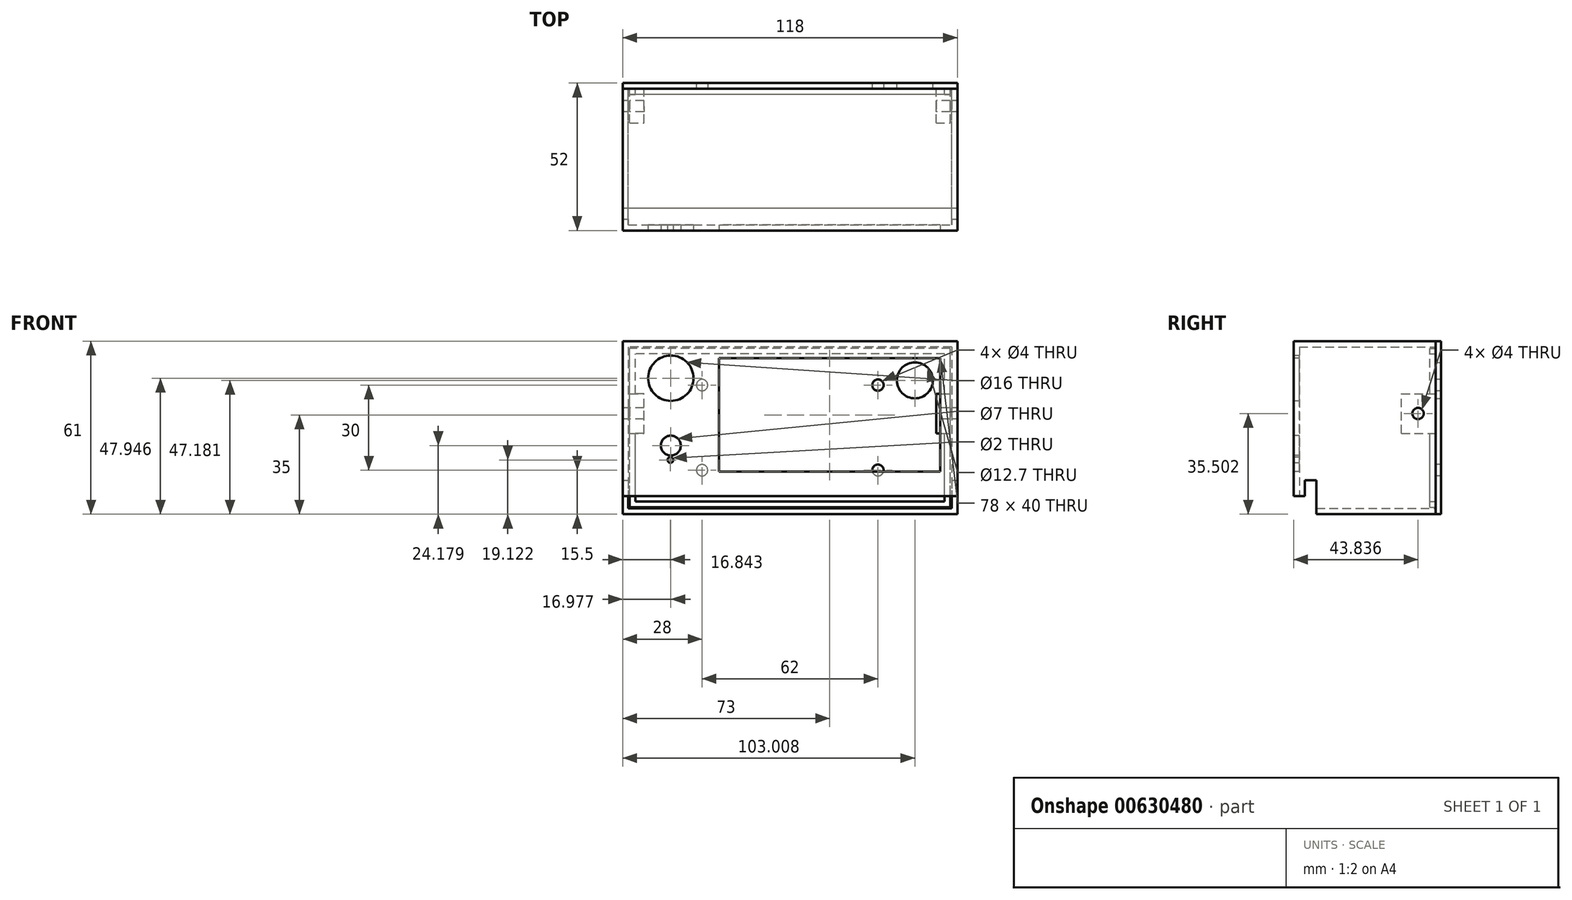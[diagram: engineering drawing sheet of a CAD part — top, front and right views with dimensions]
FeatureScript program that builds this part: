
annotation { "Feature Type Name" : "Feature", "Feature Type Description" : "" }
export const myFeature = defineFeature(function(context is Context, id is Id, definition is map)
    precondition{}
    {
        {
            var Q0;
            Q0=qCreatedBy(makeId("Top.planeOp"),FACE);
            var sketch = newSketch(context, id + "F0", { "sketchPlane" : qUnion([Q0])});
            skLineSegment(sketch, "E0.bottom", {"start": v(59, -25) * mm, "end": v(-59, -25) * mm});
            skLineSegment(sketch, "E0.top", {"start": v(59, 25) * mm, "end": v(-59, 25) * mm});
            skLineSegment(sketch, "E0.left", {"start": v(59, -25) * mm, "end": v(59, 25) * mm});
            skLineSegment(sketch, "E0.right", {"start": v(-59, -25) * mm, "end": v(-59, 25) * mm});
            skPoint(sketch, "E0.middle", {"position": v(0, 0) * mm});
            skSolve(sketch);
        }
        {
            var Q0;
            Q0 = qSketchRegion(id + "F0", true);
            extrude(context, id + "F1", {"entities" : qUnion([Q0]), "depth" : 61 * mm, "offsetDistance" : 25 * mm});
        }
        {
            var Q0;
            Q0=makeQuery(id+"F1.opExtrude","SWEPT_FACE",FACE,{"disambiguationData":[OSD([sQuery(id+"F0.wireOp",EDGE,"E0.bottom")])]});
            var sketch = newSketch(context, id + "F2", { "sketchPlane" : qUnion([Q0])});
            skLineSegment(sketch, "E1", {"start": v(59, 0) * mm, "end": v(53, 0) * mm});
            skLineSegment(sketch, "E2.bottom", {"start": v(53, 15) * mm, "end": v(-25, 15) * mm});
            skLineSegment(sketch, "E2.top", {"start": v(53, 55) * mm, "end": v(-25, 55) * mm});
            skLineSegment(sketch, "E2.left", {"start": v(53, 15) * mm, "end": v(53, 55) * mm});
            skLineSegment(sketch, "E2.right", {"start": v(-25, 15) * mm, "end": v(-25, 55) * mm});
            skCircle(sketch, "E3", {"center": v(-42.02, 24.18) * mm, "radius": 12.03 * mm});
            skCircle(sketch, "E4", {"center": v(-42.02, 24.18) * mm, "radius": 3.5 * mm});
            skCircle(sketch, "E5", {"center": v(-42.02, 47.95) * mm, "radius": 8 * mm});
            skCircle(sketch, "E6", {"center": v(-42.02, 24.18) * mm, "radius": 9.14 * mm});
            skSolve(sketch);
        }
        {
            var Q0;
            Q0=makeQuery(id+"F4.boolean.opBoolean","COPY",FACE,{"derivedFrom":makeQuery(id+"F4.opExtrude","SWEPT_FACE",FACE,{"disambiguationData":[OSD([sQuery(id+"F2.wireOp",EDGE,"E2.right")])]})});
            var Q1;
            Q1=makeQuery(id+"F1.opExtrude","SWEPT_FACE",FACE,{"disambiguationData":[OSD([sQuery(id+"F0.wireOp",EDGE,"E0.top")])]});
            shell(context, id + "F3", {"entities" : qUnion([Q0, Q1]), "thickness" : 2 * mm});
        }
        {
            var Q0;
            Q0=makeQuery(id+"F2.imprint","IMPRINT",FACE,{"disambiguationData":[TD([[makeQuery(id+"F2.imprint","IMPRINT",EDGE,{"derivedFrom":sQuery(id+"F2.wireOp",EDGE,"E5")}),1.0]])]});
            var Q1;
            Q1=makeQuery(id+"F2.imprint","IMPRINT",FACE,{"disambiguationData":[TD([[makeQuery(id+"F2.imprint","IMPRINT",EDGE,{"derivedFrom":sQuery(id+"F2.wireOp",EDGE,"E4")}),1.0]])]});
            var Q2;
            Q2=makeQuery(id+"F2.imprint","IMPRINT",FACE,{"disambiguationData":[TD([[makeQuery(id+"F2.imprint","IMPRINT",EDGE,{"derivedFrom":sQuery(id+"F2.wireOp",EDGE,"E2.bottom")}),-1.0]])]});
            extrude(context, id + "F4", {"entities" : qUnion([Q0, Q1, Q2]), "operationType" : NewBodyOperationType.REMOVE, "oppositeDirection" : true, "depth" : 48 * mm, "offsetDistance" : 25 * mm});
        }
        {
            var Q0;
            Q0=makeQuery(id+"F1.opExtrude","SWEPT_FACE",FACE,{"disambiguationData":[OSD([sQuery(id+"F0.wireOp",EDGE,"E0.left")])]});
            var sketch = newSketch(context, id + "F5", { "sketchPlane" : qUnion([Q0])});
            skLineSegment(sketch, "E7", {"start": v(-25, 0) * mm, "end": v(-21, 0) * mm});
            skLineSegment(sketch, "E8", {"start": v(-21, 0) * mm, "end": v(-21, 5) * mm});
            skLineSegment(sketch, "E9.top", {"start": v(-21, 0) * mm, "end": v(-17, 0) * mm});
            skLineSegment(sketch, "E9.left", {"start": v(-21, 5) * mm, "end": v(-21, 0) * mm});
            skLineSegment(sketch, "E9.right", {"start": v(-17, 5) * mm, "end": v(-17, 0) * mm});
            skLineSegment(sketch, "E10", {"start": v(-21, 5) * mm, "end": v(-21, 12) * mm});
            skLineSegment(sketch, "E11", {"start": v(-17, 5) * mm, "end": v(-17, 12) * mm});
            skLineSegment(sketch, "E12", {"start": v(-17, 12) * mm, "end": v(-21, 12) * mm});
            skSolve(sketch);
        }
        {
            var Q0;
            Q0=makeQuery(id+"F5.imprint","IMPRINT",FACE,{"disambiguationData":[TD([[makeQuery(id+"F5.imprint","IMPRINT",EDGE,{"derivedFrom":sQuery(id+"F5.wireOp",EDGE,"E9.bottom")}),-1.0]])]});
            var Q1;
            Q1=makeQuery(id+"F5.imprint","IMPRINT",FACE,{"disambiguationData":[TD([[makeQuery(id+"F5.imprint","IMPRINT",EDGE,{"derivedFrom":sQuery(id+"F5.wireOp",EDGE,"E9.top")}),1.0]])]});
            extrude(context, id + "F6", {"entities" : qUnion([Q0, Q1]), "operationType" : NewBodyOperationType.REMOVE, "oppositeDirection" : true, "depth" : 193.9 * mm, "offsetDistance" : 25 * mm});
        }
        {
            var Q0;
            {var subQ0=sQuery(id+"F0.wireOp",EDGE,"E0.bottom");var subQ1=sQuery(id+"F0.wireOp",EDGE,"E0.right");var subQ2=sQuery(id+"F0.wireOp",EDGE,"E0.left");Q0=makeQuery(id+"F6.boolean.opBoolean","SPLIT",FACE,{"disambiguationData":[TD([makeQuery(id+"F1.opExtrude","SWEPT_FACE",FACE,{"disambiguationData":[OSD([subQ0])]})])],"derivedFrom":makeQuery(id+"F1.opExtrude","CAP_FACE",FACE,{"disambiguationData":[OSD([subQ0,sQuery(id+"F0.wireOp",EDGE,"E0.top"),subQ2,subQ1])],"isStart":true})});}
            var sketch = newSketch(context, id + "F7", { "sketchPlane" : qUnion([Q0])});
            skSolve(sketch);
        }
        {
            var Q0;
            Q0 = qSketchRegion(id + "F7", true);
            var Q1;
            {var subQ0=sQuery(id+"F0.wireOp",EDGE,"E0.bottom");Q1=makeQuery(id+"F7.imprint","IMPRINT",FACE,{"disambiguationData":[TD([[makeQuery(id+"F7.imprint","IMPRINT",EDGE,{"derivedFrom":makeQuery(id+"F1.opExtrude","CAP_EDGE",EDGE,{"disambiguationData":[OSD([subQ0])],"isStart":true})}),1.0]])]});}
            extrude(context, id + "F8", {"entities" : qUnion([Q0, Q1]), "operationType" : NewBodyOperationType.REMOVE, "oppositeDirection" : true, "depth" : 6.4 * mm, "offsetDistance" : 25 * mm});
        }
        {
            var Q0;
            Q0=makeQuery(id+"F1.opExtrude","SWEPT_FACE",FACE,{"disambiguationData":[OSD([sQuery(id+"F0.wireOp",EDGE,"E0.top")])]});
            var sketch = newSketch(context, id + "F9", { "sketchPlane" : qUnion([Q0])});
            skLineSegment(sketch, "E13.bottom", {"start": v(-59, 61) * mm, "end": v(59, 61) * mm});
            skLineSegment(sketch, "E13.top", {"start": v(-59, 0) * mm, "end": v(59, 0) * mm});
            skLineSegment(sketch, "E13.left", {"start": v(-59, 61) * mm, "end": v(-59, 0) * mm});
            skLineSegment(sketch, "E13.right", {"start": v(59, 61) * mm, "end": v(59, 0) * mm});
            skSolve(sketch);
        }
        {
            var Q0;
            Q0 = qSketchRegion(id + "F9", true);
            extrude(context, id + "F10", {"entities" : qUnion([Q0]), "depth" : 2 * mm, "offsetDistance" : 25 * mm});
        }
        {
            var Q0;
            Q0=makeQuery(id+"F10.opExtrude","CAP_FACE",FACE,{"disambiguationData":[OSD([sQuery(id+"F9.wireOp",EDGE,"E13.bottom"),sQuery(id+"F9.wireOp",EDGE,"E13.top"),sQuery(id+"F9.wireOp",EDGE,"E13.left"),sQuery(id+"F9.wireOp",EDGE,"E13.right")])],"isStart":false});
            shell(context, id + "F11", {"entities" : qUnion([Q0]), "thickness" : 2 * mm});
        }
        {
            var Q0;
            Q0=makeQuery(id+"F10.opExtrude","CAP_FACE",FACE,{"disambiguationData":[OSD([sQuery(id+"F9.wireOp",EDGE,"E13.bottom"),sQuery(id+"F9.wireOp",EDGE,"E13.top"),sQuery(id+"F9.wireOp",EDGE,"E13.left"),sQuery(id+"F9.wireOp",EDGE,"E13.right")])],"isStart":true});
            var sketch = newSketch(context, id + "F12", { "sketchPlane" : qUnion([Q0])});
            skLineSegment(sketch, "E14.bottom", {"start": v(-59, 61) * mm, "end": v(-56.5, 61) * mm});
            skLineSegment(sketch, "E14.top", {"start": v(-59, 58.5) * mm, "end": v(-56.5, 58.5) * mm});
            skLineSegment(sketch, "E14.left", {"start": v(-59, 61) * mm, "end": v(-59, 58.5) * mm});
            skLineSegment(sketch, "E14.right", {"start": v(-56.5, 61) * mm, "end": v(-56.5, 58.5) * mm});
            skLineSegment(sketch, "E15.bottom", {"start": v(59, 0) * mm, "end": v(56.5, 0) * mm});
            skLineSegment(sketch, "E15.top", {"start": v(59, 2.5) * mm, "end": v(56.5, 2.5) * mm});
            skLineSegment(sketch, "E15.left", {"start": v(59, 0) * mm, "end": v(59, 2.5) * mm});
            skLineSegment(sketch, "E15.right", {"start": v(56.5, 0) * mm, "end": v(56.5, 2.5) * mm});
            skLineSegment(sketch, "E16.bottom", {"start": v(56.5, 2.5) * mm, "end": v(-56.5, 2.5) * mm});
            skLineSegment(sketch, "E16.top", {"start": v(56.5, 58.5) * mm, "end": v(-56.5, 58.5) * mm});
            skLineSegment(sketch, "E16.left", {"start": v(56.5, 2.5) * mm, "end": v(56.5, 58.5) * mm});
            skLineSegment(sketch, "E16.right", {"start": v(-56.5, 2.5) * mm, "end": v(-56.5, 58.5) * mm});
            skSolve(sketch);
        }
        {
            var Q0;
            Q0=makeQuery(id+"F12.imprint","IMPRINT",FACE,{"disambiguationData":[TD([[makeQuery(id+"F12.imprint","IMPRINT",EDGE,{"derivedFrom":sQuery(id+"F12.wireOp",EDGE,"E16.bottom")}),-1.0]])]});
            extrude(context, id + "F13", {"entities" : qUnion([Q0]), "operationType" : NewBodyOperationType.ADD, "depth" : 2 * mm, "offsetDistance" : 25 * mm});
        }
        {
            var Q0;
            Q0=makeQuery(id+"F13.opExtrude","CAP_FACE",FACE,{"disambiguationData":[OSD([sQuery(id+"F12.wireOp",EDGE,"E16.bottom"),sQuery(id+"F12.wireOp",EDGE,"E16.top"),sQuery(id+"F12.wireOp",EDGE,"E16.left"),sQuery(id+"F12.wireOp",EDGE,"E16.right")])],"isStart":false});
            shell(context, id + "F14", {"entities" : qUnion([Q0]), "thickness" : 2 * mm});
        }
        {
            var Q0;
            Q0=makeQuery(id+"F14.opShell","OFFSET_FACE",FACE,{"disambiguationData":[OSD([sQuery(id+"F9.wireOp",EDGE,"E13.bottom"),sQuery(id+"F9.wireOp",EDGE,"E13.top"),sQuery(id+"F9.wireOp",EDGE,"E13.left"),sQuery(id+"F9.wireOp",EDGE,"E13.right")])]});
            var sketch = newSketch(context, id + "F15", { "sketchPlane" : qUnion([Q0])});
            skPoint(sketch, "E17.endSnap0", {"position": v(0, 4.5) * mm});
            skLineSegment(sketch, "E18.bottom", {"start": v(31, 15.5) * mm, "end": v(-31, 15.5) * mm});
            skLineSegment(sketch, "E18.top", {"start": v(31, 45.5) * mm, "end": v(-31, 45.5) * mm});
            skLineSegment(sketch, "E18.left", {"start": v(31, 15.5) * mm, "end": v(31, 45.5) * mm});
            skLineSegment(sketch, "E18.right", {"start": v(-31, 15.5) * mm, "end": v(-31, 45.5) * mm});
            skPoint(sketch, "E18.middle", {"position": v(0, 30.5) * mm});
            skSolve(sketch);
        }
        {
            var Q0;
            Q0=sQuery(id+"F15.wireOp",VERTEX,"E18.right.end");
            var Q1;
            Q1=sQuery(id+"F15.wireOp",VERTEX,"E18.left.end");
            var Q2;
            Q2=sQuery(id+"F15.wireOp",VERTEX,"E18.bottom.start");
            var Q3;
            Q3=sQuery(id+"F15.wireOp",VERTEX,"E18.bottom.end");
            var Q4;
            Q4=makeQuery(id+"F10.opExtrude","SWEPT_BODY",BODY,{"disambiguationData":[OSD([sQuery(id+"F9.wireOp",EDGE,"E13.bottom"),sQuery(id+"F9.wireOp",EDGE,"E13.top"),sQuery(id+"F9.wireOp",EDGE,"E13.left"),sQuery(id+"F9.wireOp",EDGE,"E13.right")])]});
            hole(context, id + "F16", {"style" : HoleStyle.SIMPLE, "endStyle" : HoleEndStyle.THROUGH, "holeDiameter" : 4 * mm, "majorDiameter" : 5 * mm, "isTappedThrough" : true, "tappedDepth" : 12 * mm, "tapClearance" : 3, "startFromSketch" : true, "locations" : qUnion([Q0, Q1, Q2, Q3]), "scope" : qUnion([Q4])});
        }
        {
            var Q0;
            Q0=makeQuery(id+"F13.opExtrude","CAP_FACE",FACE,{"disambiguationData":[OSD([sQuery(id+"F12.wireOp",EDGE,"E16.bottom"),sQuery(id+"F12.wireOp",EDGE,"E16.top"),sQuery(id+"F12.wireOp",EDGE,"E16.left"),sQuery(id+"F12.wireOp",EDGE,"E16.right")])],"isStart":false});
            var sketch = newSketch(context, id + "F17", { "sketchPlane" : qUnion([Q0])});
            skLineSegment(sketch, "E19.bottom", {"start": v(-56.5, 30.5) * mm, "end": v(56.5, 30.5) * mm});
            skLineSegment(sketch, "E19.top", {"start": v(-56.5, 40.86) * mm, "end": v(56.5, 40.86) * mm});
            skLineSegment(sketch, "E19.left", {"start": v(-56.5, 30.5) * mm, "end": v(-56.5, 40.86) * mm});
            skLineSegment(sketch, "E19.right", {"start": v(56.5, 30.5) * mm, "end": v(56.5, 40.86) * mm});
            skSolve(sketch);
        }
        {
            var Q0;
            {var subQ0=sQuery(id+"F17.wireOp",EDGE,"E19.left");Q0=makeQuery(id+"F17.imprint","IMPRINT",FACE,{"disambiguationData":[TD([[makeQuery(id+"F17.imprint","IMPRINT",EDGE,{"derivedFrom":subQ0}),-1.0]])]});}
            var Q1;
            {var subQ0=sQuery(id+"F17.wireOp",EDGE,"E19.right");Q1=makeQuery(id+"F17.imprint","IMPRINT",FACE,{"disambiguationData":[TD([[makeQuery(id+"F17.imprint","IMPRINT",EDGE,{"derivedFrom":subQ0}),1.0]])]});}
            extrude(context, id + "F18", {"entities" : qUnion([Q0, Q1]), "operationType" : NewBodyOperationType.ADD, "depth" : 10 * mm, "offsetDistance" : 25 * mm});
        }
        {
            var Q0;
            {var subQ0=sQuery(id+"F12.wireOp",EDGE,"E16.right");Q0=makeQuery(id+"F18.boolean.opBoolean","MERGE",FACE,{"derivedFrom":[makeQuery(id+"F14.opShell","OFFSET_FACE",FACE,{"disambiguationData":[OSD([subQ0])]}),makeQuery(id+"F18.opExtrude","SWEPT_FACE",FACE,{"disambiguationData":[OSD([subQ0])]})]});}
            var sketch = newSketch(context, id + "F19", { "sketchPlane" : qUnion([Q0])});
            skLineSegment(sketch, "E20.bottom", {"start": v(13, 40.86) * mm, "end": v(25, 40.86) * mm});
            skLineSegment(sketch, "E20.top", {"start": v(13, 30.5) * mm, "end": v(25, 30.5) * mm});
            skLineSegment(sketch, "E20.left", {"start": v(13, 40.86) * mm, "end": v(13, 30.5) * mm});
            skLineSegment(sketch, "E20.right", {"start": v(25, 40.86) * mm, "end": v(25, 30.5) * mm});
            skSolve(sketch);
        }
        {
            var Q0;
            {var subQ14=sQuery(id+"F19.wireOp",EDGE,"E20.left");Q0=makeQuery(id+"F19.imprint","IMPRINT",FACE,{"disambiguationData":[TD([[makeQuery(id+"F19.imprint","IMPRINT",EDGE,{"derivedFrom":subQ14}),-1.0]])]});}
            extrude(context, id + "F20", {"entities" : qUnion([Q0]), "operationType" : NewBodyOperationType.ADD, "depth" : 1 * mm, "offsetDistance" : 25 * mm});
        }
        {
            var Q0;
            {var subQ0=sQuery(id+"F12.wireOp",EDGE,"E16.left");Q0=makeQuery(id+"F18.boolean.opBoolean","MERGE",FACE,{"derivedFrom":[makeQuery(id+"F14.opShell","OFFSET_FACE",FACE,{"disambiguationData":[OSD([subQ0])]}),makeQuery(id+"F18.opExtrude","SWEPT_FACE",FACE,{"disambiguationData":[OSD([subQ0])]})]});}
            var sketch = newSketch(context, id + "F21", { "sketchPlane" : qUnion([Q0])});
            skLineSegment(sketch, "E21.bottom", {"start": v(-13, 40.86) * mm, "end": v(-25, 40.86) * mm});
            skLineSegment(sketch, "E21.top", {"start": v(-13, 30.5) * mm, "end": v(-25, 30.5) * mm});
            skLineSegment(sketch, "E21.left", {"start": v(-13, 40.86) * mm, "end": v(-13, 30.5) * mm});
            skLineSegment(sketch, "E21.right", {"start": v(-25, 40.86) * mm, "end": v(-25, 30.5) * mm});
            skSolve(sketch);
        }
        {
            var Q0;
            Q0 = qSketchRegion(id + "F21", true);
            extrude(context, id + "F22", {"entities" : qUnion([Q0]), "operationType" : NewBodyOperationType.ADD, "depth" : 1 * mm, "offsetDistance" : 25 * mm});
        }
        {
            var Q0;
            Q0=makeQuery(id+"F20.opExtrude","CAP_FACE",FACE,{"disambiguationData":[OSD([sQuery(id+"F19.wireOp",EDGE,"E20.bottom"),sQuery(id+"F19.wireOp",EDGE,"E20.top"),sQuery(id+"F19.wireOp",EDGE,"E20.left"),sQuery(id+"F19.wireOp",EDGE,"E20.right")])],"isStart":false});
            var sketch = newSketch(context, id + "F23", { "sketchPlane" : qUnion([Q0])});
            skPoint(sketch, "E22", {"position": v(18.83, 35.66) * mm});
            skSolve(sketch);
        }
        {
            var Q0;
            Q0=makeQuery(id+"F1.opExtrude","SWEPT_FACE",FACE,{"disambiguationData":[OSD([sQuery(id+"F0.wireOp",EDGE,"E0.right")])]});
            var sketch = newSketch(context, id + "F24", { "sketchPlane" : qUnion([Q0])});
            skPoint(sketch, "E23", {"position": v(-18.84, 35.5) * mm});
            skSolve(sketch);
        }
        {
            var Q0;
            Q0=makeQuery(id+"F23.imprint","IMPRINT",FACE,{"disambiguationData":[TD([[makeQuery(id+"F23.imprint","IMPRINT",EDGE,{"derivedFrom":makeQuery(id+"F20.opExtrude","CAP_EDGE",EDGE,{"disambiguationData":[OSD([sQuery(id+"F19.wireOp",EDGE,"E20.bottom")])],"isStart":false})}),-1.0]])]});
            var Q1;
            Q1=makeQuery(id+"F22.opExtrude","CAP_FACE",FACE,{"disambiguationData":[OSD([sQuery(id+"F21.wireOp",EDGE,"E21.bottom"),sQuery(id+"F21.wireOp",EDGE,"E21.top"),sQuery(id+"F21.wireOp",EDGE,"E21.left"),sQuery(id+"F21.wireOp",EDGE,"E21.right")])],"isStart":false});
            extrude(context, id + "F25", {"entities" : qUnion([Q0, Q1]), "operationType" : NewBodyOperationType.ADD, "depth" : 2 * mm, "offsetDistance" : 25 * mm, "hasSecondDirection" : true, "secondDirectionOppositeDirection" : true, "secondDirectionDepth" : 2 * mm});
        }
        {
            var Q0;
            {var subQ0=sQuery(id+"F19.wireOp",EDGE,"E20.top");var subQ1=sQuery(id+"F17.wireOp",EDGE,"E19.bottom");var subQ2=sQuery(id+"F12.wireOp",EDGE,"E16.right");Q0=makeQuery(id+"F25.boolean.opBoolean","MERGE",FACE,{"derivedFrom":[makeQuery(id+"F20.boolean.opBoolean","MERGE",FACE,{"derivedFrom":[makeQuery(id+"F18.opExtrude","SWEPT_FACE",FACE,{"disambiguationData":[OSD([subQ1]),TDD([makeQuery(id+"F17.imprint","IMPRINT",EDGE,{"disambiguationData":[TD([[makeQuery(id+"F17.imprint","INTERSECT",VERTEX,{"derivedFrom":[makeQuery(id+"F14.opShell","OFFSET_EDGE",EDGE,{"disambiguationData":[OSD([subQ2])]}),subQ1]}),1.0]])],"derivedFrom":subQ1})])]}),makeQuery(id+"F20.opExtrude","SWEPT_FACE",FACE,{"disambiguationData":[OSD([subQ0])]})]}),makeQuery(id+"F25.opExtrude","SWEPT_FACE",FACE,{"disambiguationData":[OSD([subQ0])]})]});}
            var Q1;
            {var subQ0=sQuery(id+"F21.wireOp",EDGE,"E21.top");var subQ1=sQuery(id+"F17.wireOp",EDGE,"E19.bottom");var subQ2=sQuery(id+"F12.wireOp",EDGE,"E16.left");Q1=makeQuery(id+"F25.boolean.opBoolean","MERGE",FACE,{"derivedFrom":[makeQuery(id+"F22.boolean.opBoolean","MERGE",FACE,{"derivedFrom":[makeQuery(id+"F18.opExtrude","SWEPT_FACE",FACE,{"disambiguationData":[OSD([subQ1]),TDD([makeQuery(id+"F17.imprint","IMPRINT",EDGE,{"disambiguationData":[TD([[makeQuery(id+"F17.imprint","INTERSECT",VERTEX,{"derivedFrom":[makeQuery(id+"F14.opShell","OFFSET_EDGE",EDGE,{"disambiguationData":[OSD([subQ2])]}),subQ1]}),-1.0]])],"derivedFrom":subQ1})])]}),makeQuery(id+"F22.opExtrude","SWEPT_FACE",FACE,{"disambiguationData":[OSD([subQ0])]})]}),makeQuery(id+"F25.opExtrude","SWEPT_FACE",FACE,{"disambiguationData":[OSD([subQ0])]})]});}
            extrude(context, id + "F26", {"entities" : qUnion([Q0, Q1]), "operationType" : NewBodyOperationType.ADD, "depth" : 2 * mm, "offsetDistance" : 25 * mm, "hasSecondDirection" : true, "secondDirectionOppositeDirection" : true, "secondDirectionDepth" : 12 * mm});
        }
        {
            var Q0;
            Q0=sQuery(id+"F24.wireOp",VERTEX,"E23");
            var Q1;
            Q1=makeQuery(id+"F1.opExtrude","SWEPT_BODY",BODY,{"disambiguationData":[OSD([sQuery(id+"F0.wireOp",EDGE,"E0.bottom"),sQuery(id+"F0.wireOp",EDGE,"E0.top"),sQuery(id+"F0.wireOp",EDGE,"E0.left"),sQuery(id+"F0.wireOp",EDGE,"E0.right")])]});
            var Q2;
            Q2=makeQuery(id+"F10.opExtrude","SWEPT_BODY",BODY,{"disambiguationData":[OSD([sQuery(id+"F9.wireOp",EDGE,"E13.bottom"),sQuery(id+"F9.wireOp",EDGE,"E13.top"),sQuery(id+"F9.wireOp",EDGE,"E13.left"),sQuery(id+"F9.wireOp",EDGE,"E13.right")])]});
            hole(context, id + "F27", {"style" : HoleStyle.SIMPLE, "endStyle" : HoleEndStyle.THROUGH, "holeDiameter" : 4 * mm, "majorDiameter" : 5 * mm, "isTappedThrough" : true, "tappedDepth" : 12 * mm, "tapClearance" : 3, "locations" : qUnion([Q0]), "scope" : qUnion([Q1, Q2])});
        }
        {
            var Q0;
            Q0=makeQuery(id+"F1.opExtrude","SWEPT_FACE",FACE,{"disambiguationData":[OSD([sQuery(id+"F0.wireOp",EDGE,"E0.bottom")])]});
            var sketch = newSketch(context, id + "F28", { "sketchPlane" : qUnion([Q0])});
            skPoint(sketch, "E24", {"position": v(-42.16, 19.12) * mm});
            skSolve(sketch);
        }
        {
            var Q0;
            Q0=sQuery(id+"F28.wireOp",VERTEX,"E24");
            var Q1;
            Q1=makeQuery(id+"F1.opExtrude","SWEPT_BODY",BODY,{"disambiguationData":[OSD([sQuery(id+"F0.wireOp",EDGE,"E0.bottom"),sQuery(id+"F0.wireOp",EDGE,"E0.top"),sQuery(id+"F0.wireOp",EDGE,"E0.left"),sQuery(id+"F0.wireOp",EDGE,"E0.right")])]});
            var Q2;
            Q2=makeQuery(id+"F10.opExtrude","SWEPT_BODY",BODY,{"disambiguationData":[OSD([sQuery(id+"F9.wireOp",EDGE,"E13.bottom"),sQuery(id+"F9.wireOp",EDGE,"E13.top"),sQuery(id+"F9.wireOp",EDGE,"E13.left"),sQuery(id+"F9.wireOp",EDGE,"E13.right")])]});
            hole(context, id + "F29", {"style" : HoleStyle.SIMPLE, "endStyle" : HoleEndStyle.BLIND, "holeDiameter" : 2 * mm, "majorDiameter" : 5 * mm, "holeDepth" : 20 * mm, "isTappedThrough" : true, "tappedDepth" : 12 * mm, "tapClearance" : 3, "locations" : qUnion([Q0]), "scope" : qUnion([Q1, Q2])});
        }
        {
            var Q0;
            Q0=makeQuery(id+"F10.opExtrude","CAP_FACE",FACE,{"disambiguationData":[OSD([sQuery(id+"F9.wireOp",EDGE,"E13.bottom"),sQuery(id+"F9.wireOp",EDGE,"E13.top"),sQuery(id+"F9.wireOp",EDGE,"E13.left"),sQuery(id+"F9.wireOp",EDGE,"E13.right")])],"isStart":false});
            var sketch = newSketch(context, id + "F30", { "sketchPlane" : qUnion([Q0])});
            skPoint(sketch, "E25", {"position": v(-44, 47.18) * mm});
            skSolve(sketch);
        }
        {
            var Q0;
            Q0=sQuery(id+"F30.wireOp",VERTEX,"E25");
            var Q1;
            Q1=makeQuery(id+"F10.opExtrude","SWEPT_BODY",BODY,{"disambiguationData":[OSD([sQuery(id+"F9.wireOp",EDGE,"E13.bottom"),sQuery(id+"F9.wireOp",EDGE,"E13.top"),sQuery(id+"F9.wireOp",EDGE,"E13.left"),sQuery(id+"F9.wireOp",EDGE,"E13.right")])]});
            hole(context, id + "F31", {"style" : HoleStyle.SIMPLE, "endStyle" : HoleEndStyle.BLIND, "holeDiameter" : 12.7 * mm, "majorDiameter" : 5 * mm, "holeDepth" : 20 * mm, "isTappedThrough" : true, "tappedDepth" : 12 * mm, "tapClearance" : 3, "locations" : qUnion([Q0]), "scope" : qUnion([Q1])});
        }
    });
